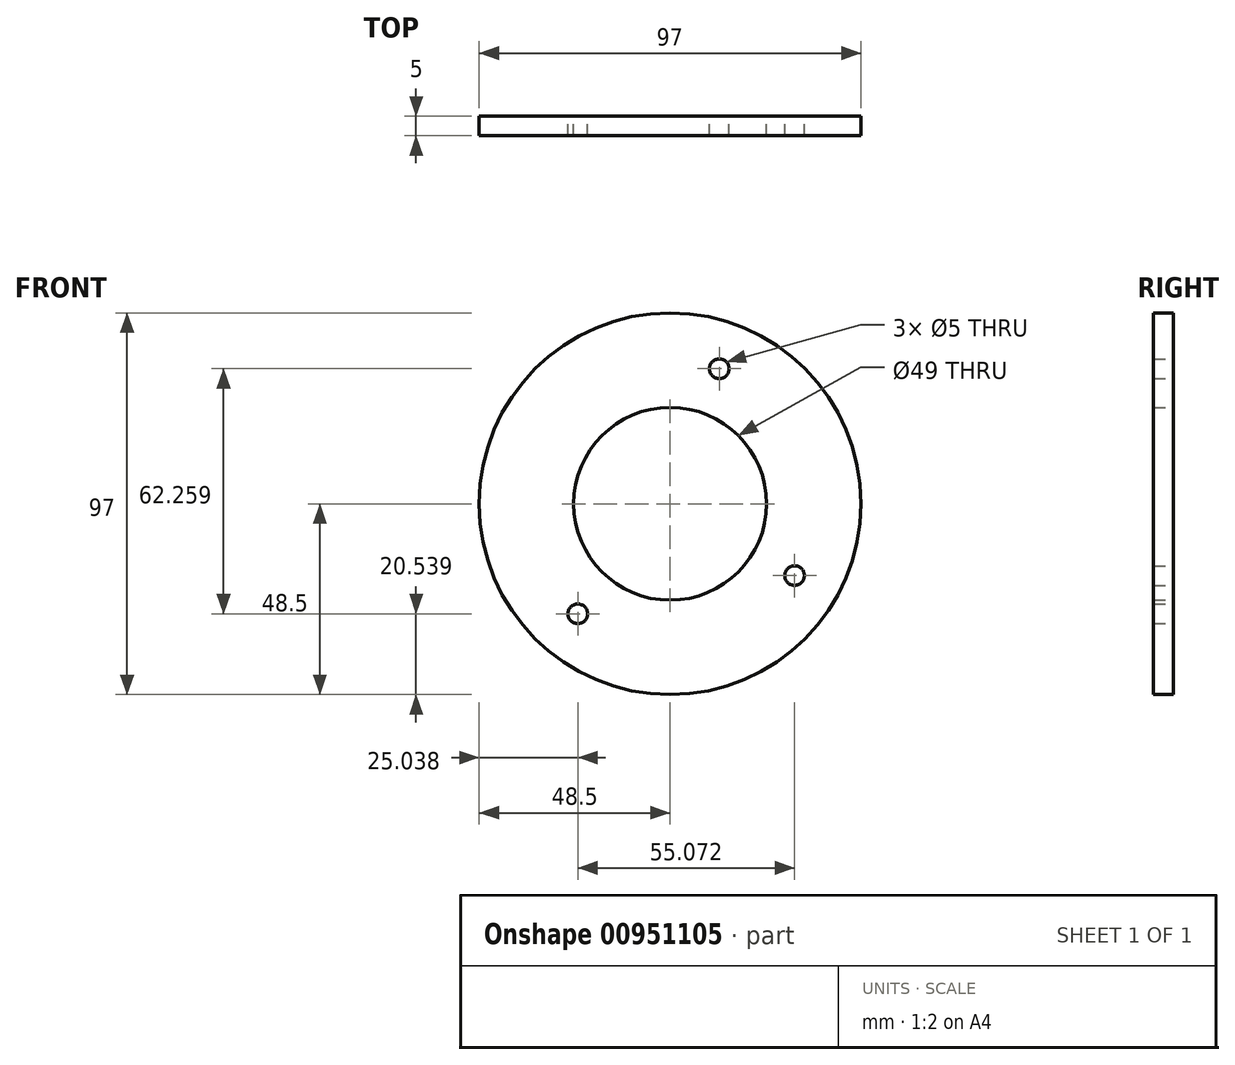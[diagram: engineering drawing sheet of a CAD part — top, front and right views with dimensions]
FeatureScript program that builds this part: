
annotation { "Feature Type Name" : "Feature", "Feature Type Description" : "" }
export const myFeature = defineFeature(function(context is Context, id is Id, definition is map)
    precondition{}
    {
        {
            var Q0;
            Q0=qCreatedBy(makeId("Front.planeOp"),FACE);
            var sketch = newSketch(context, id + "F0", { "sketchPlane" : qUnion([Q0])});
            skLineSegment(sketch, "E0", {"start": v(0, 0) * mm, "end": v(-36.5, 0) * mm});
            skLineSegment(sketch, "E1", {"start": v(-36.5, 0) * mm, "end": v(0, 0) * mm});
            skLineSegment(sketch, "E2", {"start": v(0, 0) * mm, "end": v(-23.46, -27.96) * mm});
            skCircle(sketch, "E3", {"center": v(-23.46, -27.96) * mm, "radius": 2.5 * mm});
            skLineSegment(sketch, "E4", {"start": v(0, 0) * mm, "end": v(31.6, -18.25) * mm});
            skLineSegment(sketch, "E5", {"start": v(0, 0) * mm, "end": v(12.48, 34.3) * mm});
            skCircle(sketch, "E6", {"center": v(12.48, 34.3) * mm, "radius": 2.5 * mm});
            skCircle(sketch, "E7", {"center": v(31.6, -18.25) * mm, "radius": 2.5 * mm});
            skCircle(sketch, "E8", {"center": v(0, 0) * mm, "radius": 22.5 * mm});
            skCircle(sketch, "E9", {"center": v(0, 0) * mm, "radius": 48.5 * mm});
            skCircle(sketch, "E10", {"center": v(0, 0) * mm, "radius": 24.5 * mm});
            skSolve(sketch);
        }
        {
            var Q0;
            Q0=makeQuery(id+"F0.imprint","IMPRINT",FACE,{"disambiguationData":[TD([[makeQuery(id+"F0.imprint","IMPRINT",EDGE,{"derivedFrom":sQuery(id+"F0.wireOp",EDGE,"E3")}),-1.0]])]});
            var Q1;
            Q1=sQuery(id+"F0.wireOp",EDGE,"E9");
            var Q2;
            Q2=sQuery(id+"F0.wireOp",EDGE,"E10");
            extrude(context, id + "F1", {"entities" : qUnion([Q0]), "surfaceEntities" : qUnion([Q1, Q2]), "depth" : 5 * mm, "offsetDistance" : 25 * mm});
        }
    });
